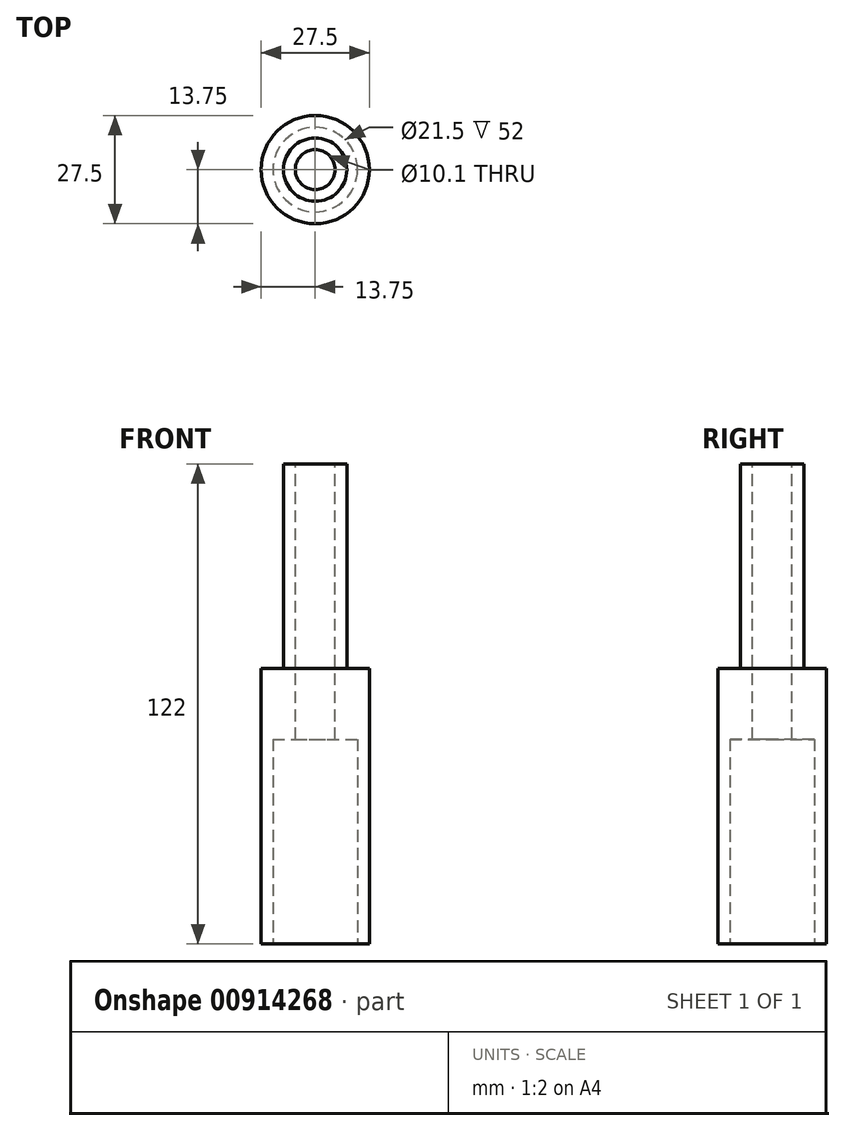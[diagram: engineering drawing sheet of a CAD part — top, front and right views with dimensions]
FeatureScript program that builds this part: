
annotation { "Feature Type Name" : "Feature", "Feature Type Description" : "" }
export const myFeature = defineFeature(function(context is Context, id is Id, definition is map)
    precondition{}
    {
        {
            var Q0;
            Q0=qCreatedBy(makeId("Top.planeOp"),FACE);
            var sketch = newSketch(context, id + "F0", { "sketchPlane" : qUnion([Q0])});
            skCircle(sketch, "E0", {"center": v(0, 0) * mm, "radius": 13.75 * mm});
            skSolve(sketch);
        }
        {
            var Q0;
            Q0 = qSketchRegion(id + "F0", true);
            extrude(context, id + "F1", {"entities" : qUnion([Q0]), "depth" : 70 * mm, "offsetDistance" : 25 * mm});
        }
        {
            var Q0;
            Q0=makeQuery(id+"F1.opExtrude","CAP_FACE",FACE,{"disambiguationData":[OSD([sQuery(id+"F0.wireOp",EDGE,"E0")])],"isStart":false});
            var sketch = newSketch(context, id + "F2", { "sketchPlane" : qUnion([Q0])});
            skCircle(sketch, "E1", {"center": v(0, 0) * mm, "radius": 8.05 * mm});
            skSolve(sketch);
        }
        {
            var Q0;
            Q0 = qSketchRegion(id + "F2", true);
            extrude(context, id + "F3", {"entities" : qUnion([Q0]), "operationType" : NewBodyOperationType.ADD, "depth" : 52 * mm, "offsetDistance" : 25 * mm});
        }
        {
            var Q0;
            Q0=makeQuery(id+"F1.opExtrude","CAP_FACE",FACE,{"disambiguationData":[OSD([sQuery(id+"F0.wireOp",EDGE,"E0")])],"isStart":true});
            var sketch = newSketch(context, id + "F4", { "sketchPlane" : qUnion([Q0])});
            skCircle(sketch, "E2", {"center": v(0, 0) * mm, "radius": 10.75 * mm});
            skSolve(sketch);
        }
        {
            var Q0;
            Q0 = qSketchRegion(id + "F4", true);
            extrude(context, id + "F5", {"entities" : qUnion([Q0]), "operationType" : NewBodyOperationType.REMOVE, "oppositeDirection" : true, "depth" : (55 - 3) * mm, "offsetDistance" : 25 * mm});
        }
        {
            var Q0;
            Q0=makeQuery(id+"F3.opExtrude","CAP_FACE",FACE,{"disambiguationData":[OSD([sQuery(id+"F2.wireOp",EDGE,"E1")])],"isStart":false});
            var sketch = newSketch(context, id + "F6", { "sketchPlane" : qUnion([Q0])});
            skCircle(sketch, "E3", {"center": v(0, 0) * mm, "radius": 5.05 * mm});
            skSolve(sketch);
        }
        {
            var Q0;
            Q0 = qSketchRegion(id + "F6", true);
            extrude(context, id + "F7", {"entities" : qUnion([Q0]), "operationType" : NewBodyOperationType.REMOVE, "endBound" : BoundingType.UP_TO_NEXT, "oppositeDirection" : true, "depth" : 52 * mm, "offsetDistance" : 25 * mm});
        }
    });
